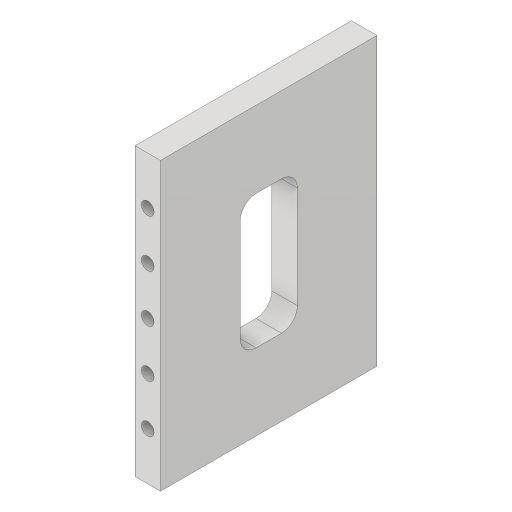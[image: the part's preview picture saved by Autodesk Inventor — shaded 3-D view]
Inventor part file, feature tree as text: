
AUTODESK INVENTOR PART (.ipt)
format: ipt  version: 2023.2 (Build 272271000, 271)  size: 161,792 bytes
history: native  units: mm
features: extrude x4, sketch x4, projected_geometry x3, other x1, fillet x1
ambient origin geometry x8: Origin, YZ Plane, XZ Plane, XY Plane, X Axis, Y Axis, Z Axis, Center Point
bodies: Body1 (feature_tree)
feature tree (13):
  other  "솔리드1"
  extrude  "돌출1"  Depth=4.0mm
  extrude  "돌출3"  Depth=45.0mm
  extrude  "돌출4"  Depth=2.0mm
  extrude  "돌출5"  Depth=22.5mm
  fillet  "모깎기1"  Radius=34.0mm
  sketch  "스케치1"
  sketch  "스케치2"
  projected_geometry  "투영된 루프1"
  sketch  "스케치3"
  projected_geometry  "투영된 루프2"
  sketch  "스케치4"
  projected_geometry  "투영된 루프3"
